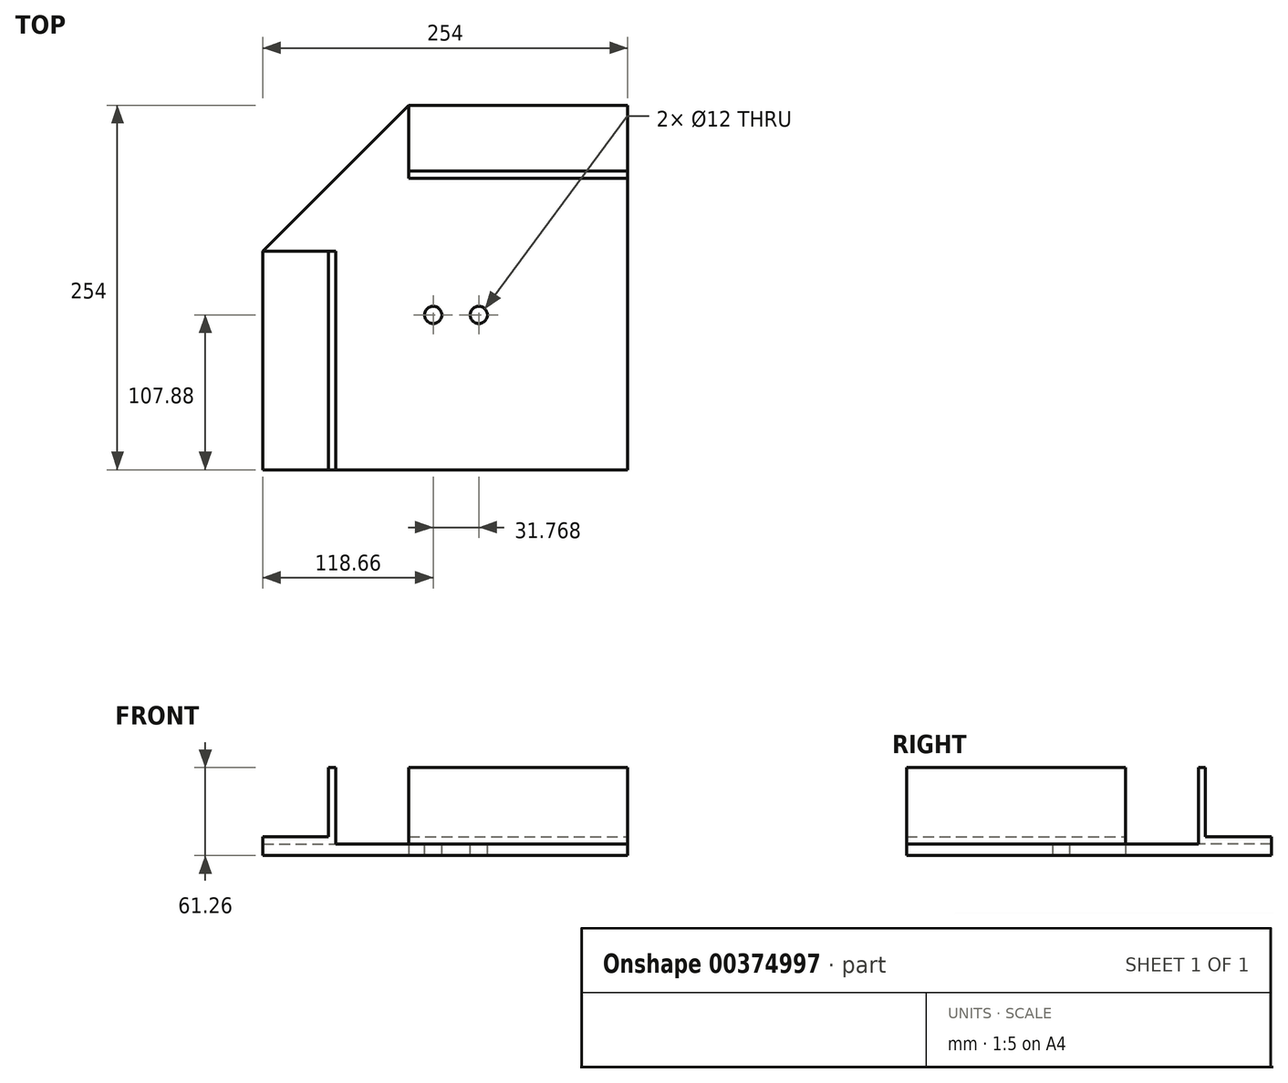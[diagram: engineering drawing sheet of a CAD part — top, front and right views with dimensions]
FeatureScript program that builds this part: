
annotation { "Feature Type Name" : "Feature", "Feature Type Description" : "" }
export const myFeature = defineFeature(function(context is Context, id is Id, definition is map)
    precondition{}
    {
        {
            var Q0;
            Q0=qCreatedBy(makeId("Top.planeOp"),FACE);
            var sketch = newSketch(context, id + "F0", { "sketchPlane" : qUnion([Q0])});
            skLineSegment(sketch, "E0", {"start": v(-111.82, 44.52) * mm, "end": v(-111.82, -107.88) * mm});
            skLineSegment(sketch, "E1", {"start": v(-111.82, -107.88) * mm, "end": v(142.18, -107.88) * mm});
            skLineSegment(sketch, "E2", {"start": v(142.18, -107.88) * mm, "end": v(142.18, 146.12) * mm});
            skLineSegment(sketch, "E3", {"start": v(142.18, 146.12) * mm, "end": v(-10.22, 146.12) * mm});
            skLineSegment(sketch, "E4", {"start": v(-10.22, 146.12) * mm, "end": v(-10.22, 146.12) * mm});
            skLineSegment(sketch, "E5", {"start": v(-111.82, 44.52) * mm, "end": v(-10.22, 146.12) * mm});
            skSolve(sketch);
        }
        {
            var Q0;
            Q0 = qSketchRegion(id + "F0", true);
            extrude(context, id + "F1", {"entities" : qUnion([Q0]), "depth" : 8 * mm});
        }
        {
            var Q0;
            Q0=makeQuery(id+"F1.opExtrude","CAP_FACE",FACE,{"disambiguationData":[OSD([sQuery(id+"F0.wireOp",EDGE,"E0"),sQuery(id+"F0.wireOp",EDGE,"E1"),sQuery(id+"F0.wireOp",EDGE,"E2"),sQuery(id+"F0.wireOp",EDGE,"E3"),sQuery(id+"F0.wireOp",EDGE,"E5")])],"isStart":false});
            var sketch = newSketch(context, id + "F2", { "sketchPlane" : qUnion([Q0])});
            skLineSegment(sketch, "E6.bottom", {"start": v(-10.22, 146.12) * mm, "end": v(142.18, 146.12) * mm});
            skLineSegment(sketch, "E6.top", {"start": v(-10.22, 95.32) * mm, "end": v(142.18, 95.32) * mm});
            skLineSegment(sketch, "E6.left", {"start": v(-10.22, 146.12) * mm, "end": v(-10.22, 95.32) * mm});
            skLineSegment(sketch, "E6.right", {"start": v(142.18, 146.12) * mm, "end": v(142.18, 95.32) * mm});
            skLineSegment(sketch, "E7.bottom", {"start": v(-111.82, 44.52) * mm, "end": v(-61.02, 44.52) * mm});
            skLineSegment(sketch, "E7.top", {"start": v(-111.82, -107.88) * mm, "end": v(-61.02, -107.88) * mm});
            skLineSegment(sketch, "E7.left", {"start": v(-111.82, 44.52) * mm, "end": v(-111.82, -107.88) * mm});
            skLineSegment(sketch, "E7.right", {"start": v(-61.02, 44.52) * mm, "end": v(-61.02, -107.88) * mm});
            skSolve(sketch);
        }
        {
            var Q0;
            Q0 = qSketchRegion(id + "F2", true);
            extrude(context, id + "F3", {"entities" : qUnion([Q0]), "operationType" : NewBodyOperationType.ADD, "depth" : 5 * mm});
        }
        {
            var Q0;
            Q0=makeQuery(id+"F3.opExtrude","CAP_FACE",FACE,{"disambiguationData":[OSD([sQuery(id+"F2.wireOp",EDGE,"E7.bottom"),sQuery(id+"F2.wireOp",EDGE,"E7.top"),sQuery(id+"F2.wireOp",EDGE,"E7.left"),sQuery(id+"F2.wireOp",EDGE,"E7.right")])],"isStart":false});
            var sketch = newSketch(context, id + "F4", { "sketchPlane" : qUnion([Q0])});
            skLineSegment(sketch, "E8.bottom", {"start": v(-61.02, -107.88) * mm, "end": v(-66.02, -107.88) * mm});
            skLineSegment(sketch, "E8.top", {"start": v(-61.02, 44.52) * mm, "end": v(-66.02, 44.52) * mm});
            skLineSegment(sketch, "E8.left", {"start": v(-61.02, -107.88) * mm, "end": v(-61.02, 44.52) * mm});
            skLineSegment(sketch, "E8.right", {"start": v(-66.02, -107.88) * mm, "end": v(-66.02, 44.52) * mm});
            skSolve(sketch);
        }
        {
            var Q0;
            Q0=makeQuery(id+"F3.opExtrude","CAP_FACE",FACE,{"disambiguationData":[OSD([sQuery(id+"F2.wireOp",EDGE,"E6.bottom"),sQuery(id+"F2.wireOp",EDGE,"E6.top"),sQuery(id+"F2.wireOp",EDGE,"E6.left"),sQuery(id+"F2.wireOp",EDGE,"E6.right")])],"isStart":false});
            var sketch = newSketch(context, id + "F5", { "sketchPlane" : qUnion([Q0])});
            skLineSegment(sketch, "E9.bottom", {"start": v(-10.22, 100.32) * mm, "end": v(142.18, 100.32) * mm});
            skLineSegment(sketch, "E9.top", {"start": v(-10.22, 95.32) * mm, "end": v(142.18, 95.32) * mm});
            skLineSegment(sketch, "E9.left", {"start": v(-10.22, 100.32) * mm, "end": v(-10.22, 95.32) * mm});
            skLineSegment(sketch, "E9.right", {"start": v(142.18, 100.32) * mm, "end": v(142.18, 95.32) * mm});
            skSolve(sketch);
        }
        {
            var Q0;
            Q0 = qSketchRegion(id + "F5", true);
            extrude(context, id + "F6", {"entities" : qUnion([Q0]), "operationType" : NewBodyOperationType.ADD, "depth" : 48.26 * mm});
        }
        {
            var Q0;
            Q0=makeQuery(id+"F1.opExtrude","CAP_FACE",FACE,{"disambiguationData":[OSD([sQuery(id+"F0.wireOp",EDGE,"E0"),sQuery(id+"F0.wireOp",EDGE,"E1"),sQuery(id+"F0.wireOp",EDGE,"E2"),sQuery(id+"F0.wireOp",EDGE,"E3"),sQuery(id+"F0.wireOp",EDGE,"E5")])],"isStart":false});
            var sketch = newSketch(context, id + "F7", { "sketchPlane" : qUnion([Q0])});
            skCircle(sketch, "E10", {"center": v(6.84, 0) * mm, "radius": 6 * mm});
            skSolve(sketch);
        }
        {
            var Q0;
            Q0 = qSketchRegion(id + "F7", true);
            extrude(context, id + "F8", {"entities" : qUnion([Q0]), "operationType" : NewBodyOperationType.REMOVE, "oppositeDirection" : true, "depth" : 8 * mm});
        }
        {
            var Q0;
            Q0=makeQuery(id+"F1.opExtrude","CAP_FACE",FACE,{"disambiguationData":[OSD([sQuery(id+"F0.wireOp",EDGE,"E0"),sQuery(id+"F0.wireOp",EDGE,"E1"),sQuery(id+"F0.wireOp",EDGE,"E2"),sQuery(id+"F0.wireOp",EDGE,"E3"),sQuery(id+"F0.wireOp",EDGE,"E5")])],"isStart":false});
            var sketch = newSketch(context, id + "F9", { "sketchPlane" : qUnion([Q0])});
            skCircle(sketch, "E11", {"center": v(38.6, 0) * mm, "radius": 6 * mm});
            skSolve(sketch);
        }
        {
            var Q0;
            Q0 = qSketchRegion(id + "F9", true);
            extrude(context, id + "F10", {"entities" : qUnion([Q0]), "operationType" : NewBodyOperationType.REMOVE, "oppositeDirection" : true, "depth" : 8 * mm});
        }
        {
            var Q0;
            Q0 = qSketchRegion(id + "F4", true);
            extrude(context, id + "F11", {"entities" : qUnion([Q0]), "operationType" : NewBodyOperationType.ADD, "depth" : 48.26 * mm});
        }
    });
